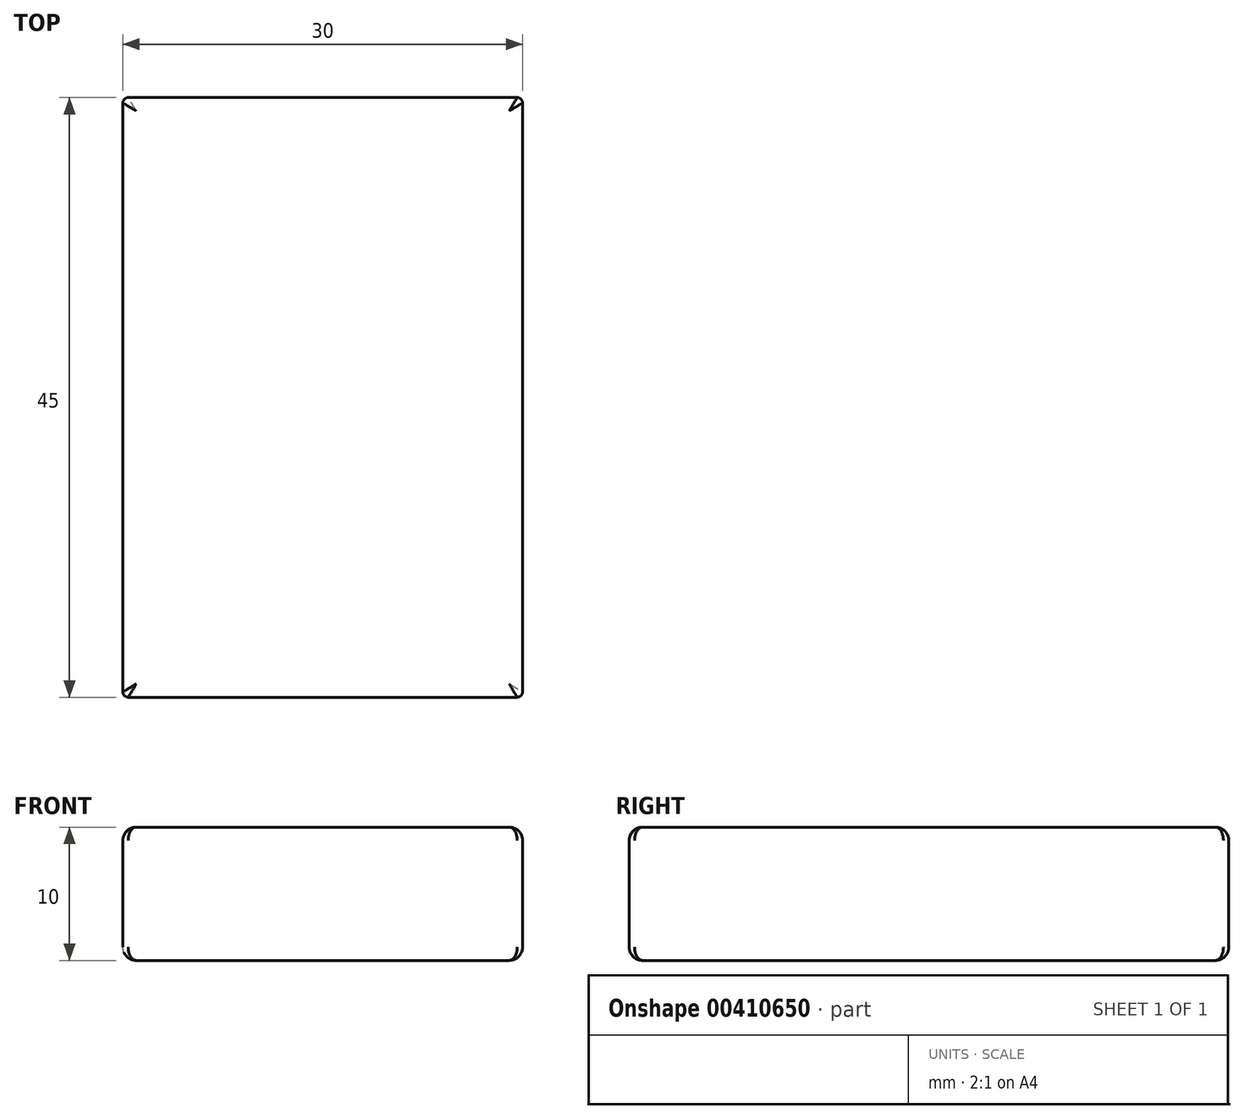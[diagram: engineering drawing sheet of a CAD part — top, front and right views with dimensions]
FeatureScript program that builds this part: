
annotation { "Feature Type Name" : "Feature", "Feature Type Description" : "" }
export const myFeature = defineFeature(function(context is Context, id is Id, definition is map)
    precondition{}
    {
        {
            var Q0;
            Q0=qCreatedBy(makeId("Top.planeOp"),FACE);
            var sketch = newSketch(context, id + "F0", { "sketchPlane" : qUnion([Q0])});
            skLineSegment(sketch, "E0.bottom", {"start": v(-15, 22.5) * mm, "end": v(15, 22.5) * mm});
            skLineSegment(sketch, "E0.top", {"start": v(-15, -22.5) * mm, "end": v(15, -22.5) * mm});
            skLineSegment(sketch, "E0.left", {"start": v(-15, 22.5) * mm, "end": v(-15, -22.5) * mm});
            skLineSegment(sketch, "E0.right", {"start": v(15, 22.5) * mm, "end": v(15, -22.5) * mm});
            skPoint(sketch, "E0.middle", {"position": v(0, 0) * mm});
            skSolve(sketch);
        }
        {
            var Q0;
            Q0 = qSketchRegion(id + "F0", true);
            extrude(context, id + "F1", {"entities" : qUnion([Q0]), "depth" : 10 * mm, "offsetDistance" : 25 * mm});
        }
        {
            var Q0;
            Q0=makeQuery(id+"F1.opExtrude","SWEPT_EDGE",EDGE,{"disambiguationData":[OSD([sQuery(id+"F0.wireOp",EDGE,"E0.top"),sQuery(id+"F0.wireOp",EDGE,"E0.left")])]});
            var Q1;
            Q1=makeQuery(id+"F1.opExtrude","SWEPT_EDGE",EDGE,{"disambiguationData":[OSD([sQuery(id+"F0.wireOp",EDGE,"E0.top"),sQuery(id+"F0.wireOp",EDGE,"E0.right")])]});
            var Q2;
            Q2=makeQuery(id+"F1.opExtrude","SWEPT_EDGE",EDGE,{"disambiguationData":[OSD([sQuery(id+"F0.wireOp",EDGE,"E0.bottom"),sQuery(id+"F0.wireOp",EDGE,"E0.right")])]});
            var Q3;
            Q3=makeQuery(id+"F1.opExtrude","SWEPT_EDGE",EDGE,{"disambiguationData":[OSD([sQuery(id+"F0.wireOp",EDGE,"E0.bottom"),sQuery(id+"F0.wireOp",EDGE,"E0.left")])]});
            fillet(context, id + "F2", {"entities" : qUnion([Q0, Q1, Q2, Q3]), "radius" : .4 * mm, "tangentPropagation" : true, "allowEdgeOverflow" : false});
        }
        {
            var Q0;
            Q0=makeQuery(id+"F1.opExtrude","CAP_FACE",FACE,{"disambiguationData":[OSD([sQuery(id+"F0.wireOp",EDGE,"E0.bottom"),sQuery(id+"F0.wireOp",EDGE,"E0.top"),sQuery(id+"F0.wireOp",EDGE,"E0.left"),sQuery(id+"F0.wireOp",EDGE,"E0.right")])],"isStart":false});
            var Q1;
            Q1=makeQuery(id+"F1.opExtrude","CAP_FACE",FACE,{"disambiguationData":[OSD([sQuery(id+"F0.wireOp",EDGE,"E0.bottom"),sQuery(id+"F0.wireOp",EDGE,"E0.top"),sQuery(id+"F0.wireOp",EDGE,"E0.left"),sQuery(id+"F0.wireOp",EDGE,"E0.right")])],"isStart":true});
            fillet(context, id + "F3", {"entities" : qUnion([Q0, Q1]), "radius" : 1 * mm, "tangentPropagation" : true, "allowEdgeOverflow" : false});
        }
    });
